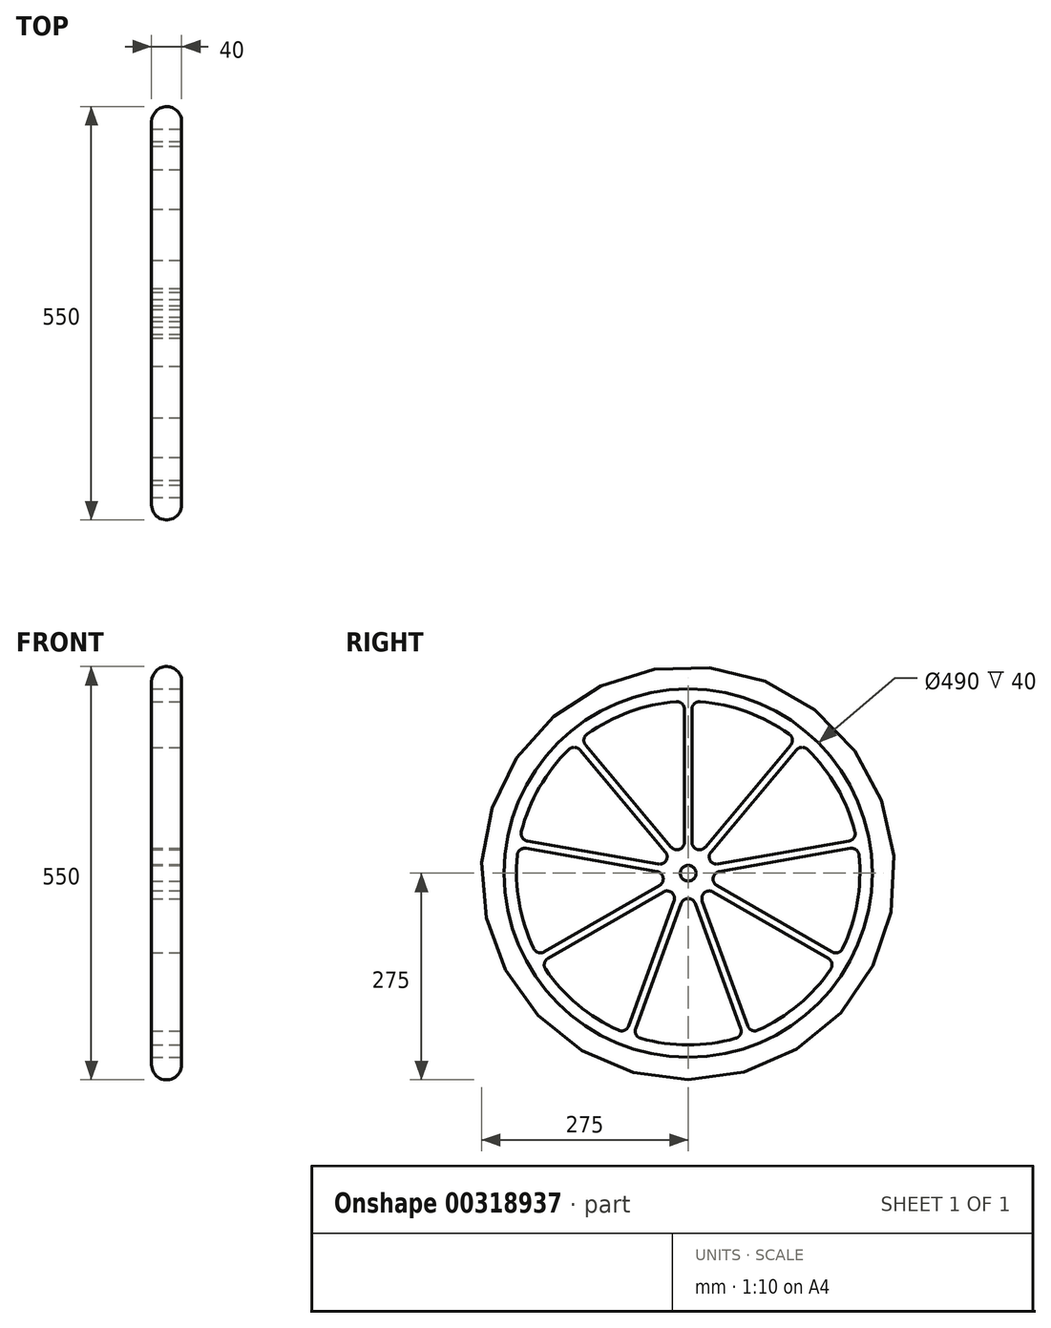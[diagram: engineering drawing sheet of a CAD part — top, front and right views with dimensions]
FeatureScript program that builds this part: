
annotation { "Feature Type Name" : "Feature", "Feature Type Description" : "" }
export const myFeature = defineFeature(function(context is Context, id is Id, definition is map)
    precondition{}
    {
        {
            var Q0;
            Q0=qCreatedBy(makeId("Front.planeOp"),FACE);
            var sketch = newSketch(context, id + "F0", { "sketchPlane" : qUnion([Q0])});
            skLineSegment(sketch, "E0.bottom", {"start": v(-20, 0) * mm, "end": v(20, 0) * mm});
            skLineSegment(sketch, "E0.top", {"start": v(-20, 245) * mm, "end": v(20, 245) * mm});
            skLineSegment(sketch, "E0.left", {"start": v(-20, 0) * mm, "end": v(-20, 245) * mm});
            skLineSegment(sketch, "E0.right", {"start": v(20, 0) * mm, "end": v(20, 245) * mm});
            skSolve(sketch);
        }
        {
            var Q0;
            Q0 = qSketchRegion(id + "F0", true);
            var Q1;
            Q1=sQuery(id+"F0.wireOp",EDGE,"E0.bottom");
            revolve(context, id + "F1", {"entities" : qUnion([Q0]), "axis" : qUnion([Q1]), "revolveType" : RevolveType.FULL});
        }
        {
            var Q0;
            Q0=makeQuery(id+"F1.opRevolve","SWEPT_FACE",FACE,{"disambiguationData":[OSD([sQuery(id+"F0.wireOp",EDGE,"E0.right")])]});
            var sketch = newSketch(context, id + "F2", { "sketchPlane" : qUnion([Q0])});
            skSolve(sketch);
        }
        {
            var Q0;
            Q0=makeQuery(id+"F2.imprint","IMPRINT",FACE,{"disambiguationData":[TD([[makeQuery(id+"F2.imprint","IMPRINT",EDGE,{"derivedFrom":makeQuery(id+"F1.opRevolve","SWEPT_EDGE",EDGE,{"disambiguationData":[OSD([sQuery(id+"F0.wireOp",EDGE,"E0.top"),sQuery(id+"F0.wireOp",EDGE,"E0.right")])]})}),-1.0]])]});
            var sketch = newSketch(context, id + "F3", { "sketchPlane" : qUnion([Q0])});
            skLineSegment(sketch, "E1", {"start": v(0, 0) * mm, "end": v(0, 260) * mm, "construction": true});
            skLineSegment(sketch, "E2", {"start": v(0, 0) * mm, "end": v(167.12, 199.17) * mm, "construction": true});
            skLineSegment(sketch, "E3", {"start": v(5, 218.19) * mm, "end": v(5, 41.21) * mm});
            skLineSegment(sketch, "E4", {"start": v(22.66, 34.78) * mm, "end": v(136.42, 170.36) * mm});
            skArc(sketch, "E5", {"start": v(134.58, 184.91) * mm, "mid": v(78.14, 214.68) * mm, "end": v(15.77, 228.16) * mm});
            skPoint(sketch, "E6.visualSharp", {"position": v(5, 13.74) * mm});
            skArc(sketch, "E6.filletArc", {"start": v(5, 41.21) * mm, "mid": v(11.58, 31.82) * mm, "end": v(22.66, 34.78) * mm});
            skPoint(sketch, "E7.visualSharp", {"position": v(143.2, 178.44) * mm});
            skArc(sketch, "E7.filletArc", {"start": v(136.42, 170.36) * mm, "mid": v(138.68, 178.04) * mm, "end": v(134.58, 184.91) * mm});
            skPoint(sketch, "E8.visualSharp", {"position": v(5, 228.74) * mm});
            skArc(sketch, "E8.filletArc", {"start": v(15.77, 228.16) * mm, "mid": v(8.2, 225.52) * mm, "end": v(5, 218.19) * mm});
            skArc(sketch, "E9.1.0", {"start": v(-15.77, 228.16) * mm, "mid": v(-78.14, 214.68) * mm, "end": v(-134.58, 184.91) * mm});
            skArc(sketch, "E9.1.1", {"start": v(-134.58, 184.91) * mm, "mid": v(-138.68, 178.04) * mm, "end": v(-136.42, 170.36) * mm});
            skLineSegment(sketch, "E9.1.2", {"start": v(-136.42, 170.36) * mm, "end": v(-22.66, 34.78) * mm});
            skArc(sketch, "E9.1.3", {"start": v(-5, 218.19) * mm, "mid": v(-8.2, 225.52) * mm, "end": v(-15.77, 228.16) * mm});
            skLineSegment(sketch, "E9.1.4", {"start": v(-5, 41.21) * mm, "end": v(-5, 218.19) * mm});
            skArc(sketch, "E9.1.5", {"start": v(-22.66, 34.78) * mm, "mid": v(-11.58, 31.82) * mm, "end": v(-5, 41.21) * mm});
            skPoint(sketch, "E9.1.6", {"position": v(-5, 13.74) * mm});
            skArc(sketch, "E9.2.0", {"start": v(-158.73, 164.64) * mm, "mid": v(-197.85, 114.23) * mm, "end": v(-221.95, 55.15) * mm});
            skArc(sketch, "E9.2.1", {"start": v(-221.95, 55.15) * mm, "mid": v(-220.67, 47.24) * mm, "end": v(-214, 42.81) * mm});
            skLineSegment(sketch, "E9.2.2", {"start": v(-214, 42.81) * mm, "end": v(-39.72, 12.08) * mm});
            skArc(sketch, "E9.2.3", {"start": v(-144.08, 163.93) * mm, "mid": v(-151.25, 167.49) * mm, "end": v(-158.73, 164.64) * mm});
            skLineSegment(sketch, "E9.2.4", {"start": v(-30.32, 28.36) * mm, "end": v(-144.08, 163.93) * mm});
            skArc(sketch, "E9.2.5", {"start": v(-39.72, 12.08) * mm, "mid": v(-29.32, 16.93) * mm, "end": v(-30.32, 28.36) * mm});
            skPoint(sketch, "E9.2.6", {"position": v(-12.66, 7.3) * mm});
            skArc(sketch, "E9.3.0", {"start": v(-227.43, 24.1) * mm, "mid": v(-224.98, -39.67) * mm, "end": v(-205.47, -100.43) * mm});
            skArc(sketch, "E9.3.1", {"start": v(-205.47, -100.43) * mm, "mid": v(-199.41, -105.66) * mm, "end": v(-191.46, -104.76) * mm});
            skLineSegment(sketch, "E9.3.2", {"start": v(-191.46, -104.76) * mm, "end": v(-38.2, -16.28) * mm});
            skArc(sketch, "E9.3.3", {"start": v(-215.74, 32.96) * mm, "mid": v(-223.52, 31.08) * mm, "end": v(-227.43, 24.1) * mm});
            skLineSegment(sketch, "E9.3.4", {"start": v(-41.45, 2.23) * mm, "end": v(-215.74, 32.96) * mm});
            skArc(sketch, "E9.3.5", {"start": v(-38.2, -16.28) * mm, "mid": v(-33.34, -5.88) * mm, "end": v(-41.45, 2.23) * mm});
            skPoint(sketch, "E9.3.6", {"position": v(-14.4, -2.54) * mm});
            skPoint(sketch, "E9.center", {"position": v(0, 0) * mm});
            skArc(sketch, "E10.1.4.0", {"start": v(-189.7, -127.73) * mm, "mid": v(-146.85, -175) * mm, "end": v(-92.85, -209) * mm});
            skArc(sketch, "E10.4.4.0", {"start": v(-92.85, -209) * mm, "mid": v(-84.84, -209.12) * mm, "end": v(-79.32, -203.32) * mm});
            skLineSegment(sketch, "E10.8.4.0", {"start": v(-79.32, -203.32) * mm, "end": v(-18.8, -37.02) * mm});
            skArc(sketch, "E10.11.4.0", {"start": v(-186.46, -113.42) * mm, "mid": v(-191.2, -119.87) * mm, "end": v(-189.7, -127.73) * mm});
            skLineSegment(sketch, "E10.15.4.0", {"start": v(-33.2, -24.94) * mm, "end": v(-186.46, -113.42) * mm});
            skArc(sketch, "E10.18.4.0", {"start": v(-18.8, -37.02) * mm, "mid": v(-21.76, -25.94) * mm, "end": v(-33.2, -24.94) * mm});
            skPoint(sketch, "E10.22.4.0", {"position": v(-9.4, -11.2) * mm});
            skArc(sketch, "E10.1.5.0", {"start": v(-63.22, -219.8) * mm, "mid": v(0, -228.45) * mm, "end": v(63.22, -219.8) * mm});
            skArc(sketch, "E10.4.5.0", {"start": v(63.22, -219.8) * mm, "mid": v(69.42, -214.73) * mm, "end": v(69.93, -206.74) * mm});
            skLineSegment(sketch, "E10.8.5.0", {"start": v(69.93, -206.74) * mm, "end": v(9.4, -40.44) * mm});
            skArc(sketch, "E10.11.5.0", {"start": v(-69.93, -206.74) * mm, "mid": v(-69.42, -214.73) * mm, "end": v(-63.22, -219.8) * mm});
            skLineSegment(sketch, "E10.15.5.0", {"start": v(-9.4, -40.44) * mm, "end": v(-69.93, -206.74) * mm});
            skArc(sketch, "E10.18.5.0", {"start": v(9.4, -40.44) * mm, "mid": v(0, -33.86) * mm, "end": v(-9.4, -40.44) * mm});
            skPoint(sketch, "E10.22.5.0", {"position": v(0, -14.62) * mm});
            skArc(sketch, "E11.1.6.0", {"start": v(92.85, -209) * mm, "mid": v(146.85, -175) * mm, "end": v(189.7, -127.73) * mm});
            skArc(sketch, "E11.4.6.0", {"start": v(189.7, -127.73) * mm, "mid": v(191.2, -119.87) * mm, "end": v(186.46, -113.42) * mm});
            skLineSegment(sketch, "E11.8.6.0", {"start": v(186.46, -113.42) * mm, "end": v(33.2, -24.94) * mm});
            skArc(sketch, "E11.11.6.0", {"start": v(79.32, -203.32) * mm, "mid": v(84.84, -209.12) * mm, "end": v(92.85, -209) * mm});
            skLineSegment(sketch, "E11.15.6.0", {"start": v(18.8, -37.02) * mm, "end": v(79.32, -203.32) * mm});
            skArc(sketch, "E11.18.6.0", {"start": v(33.2, -24.94) * mm, "mid": v(21.76, -25.94) * mm, "end": v(18.8, -37.02) * mm});
            skPoint(sketch, "E11.22.6.0", {"position": v(9.4, -11.2) * mm});
            skArc(sketch, "E11.1.7.0", {"start": v(205.47, -100.43) * mm, "mid": v(224.98, -39.67) * mm, "end": v(227.43, 24.1) * mm});
            skArc(sketch, "E11.4.7.0", {"start": v(227.43, 24.1) * mm, "mid": v(223.52, 31.08) * mm, "end": v(215.74, 32.96) * mm});
            skLineSegment(sketch, "E11.8.7.0", {"start": v(215.74, 32.96) * mm, "end": v(41.45, 2.23) * mm});
            skArc(sketch, "E11.11.7.0", {"start": v(191.46, -104.76) * mm, "mid": v(199.41, -105.66) * mm, "end": v(205.47, -100.43) * mm});
            skLineSegment(sketch, "E11.15.7.0", {"start": v(38.2, -16.28) * mm, "end": v(191.46, -104.76) * mm});
            skArc(sketch, "E11.18.7.0", {"start": v(41.45, 2.23) * mm, "mid": v(33.34, -5.88) * mm, "end": v(38.2, -16.28) * mm});
            skPoint(sketch, "E11.22.7.0", {"position": v(14.4, -2.54) * mm});
            skArc(sketch, "E11.1.8.0", {"start": v(221.95, 55.15) * mm, "mid": v(197.85, 114.23) * mm, "end": v(158.73, 164.64) * mm});
            skArc(sketch, "E11.4.8.0", {"start": v(158.73, 164.64) * mm, "mid": v(151.25, 167.49) * mm, "end": v(144.08, 163.93) * mm});
            skLineSegment(sketch, "E11.8.8.0", {"start": v(144.08, 163.93) * mm, "end": v(30.32, 28.36) * mm});
            skArc(sketch, "E11.11.8.0", {"start": v(214, 42.81) * mm, "mid": v(220.67, 47.24) * mm, "end": v(221.95, 55.15) * mm});
            skLineSegment(sketch, "E11.15.8.0", {"start": v(39.72, 12.08) * mm, "end": v(214, 42.81) * mm});
            skArc(sketch, "E11.18.8.0", {"start": v(30.32, 28.36) * mm, "mid": v(29.32, 16.93) * mm, "end": v(39.72, 12.08) * mm});
            skPoint(sketch, "E11.22.8.0", {"position": v(12.66, 7.3) * mm});
            skCircle(sketch, "E12", {"center": v(0, 0) * mm, "radius": 10.5 * mm});
            skSolve(sketch);
        }
        {
            var Q0;
            Q0 = qSketchRegion(id + "F3", true);
            extrude(context, id + "F4", {"entities" : qUnion([Q0]), "operationType" : NewBodyOperationType.REMOVE, "oppositeDirection" : true, "depth" : 79 * mm, "offsetDistance" : 25 * mm});
        }
        {
            var Q0;
            Q0=makeQuery(id+"F2.imprint","IMPRINT",FACE,{"disambiguationData":[TD([[makeQuery(id+"F2.imprint","IMPRINT",EDGE,{"derivedFrom":makeQuery(id+"F1.opRevolve","SWEPT_EDGE",EDGE,{"disambiguationData":[OSD([sQuery(id+"F0.wireOp",EDGE,"E0.top"),sQuery(id+"F0.wireOp",EDGE,"E0.right")])]})}),-1.0]])]});
            var sketch = newSketch(context, id + "F5", { "sketchPlane" : qUnion([Q0])});
            skCircle(sketch, "E13", {"center": v(0, 0) * mm, "radius": 275 * mm});
            skSolve(sketch);
        }
        {
            var Q0;
            Q0=makeQuery(id+"F5.imprint","IMPRINT",FACE,{"disambiguationData":[TD([[makeQuery(id+"F5.imprint","IMPRINT",EDGE,{"derivedFrom":sQuery(id+"F5.wireOp",EDGE,"E13")}),1.0]])]});
            extrude(context, id + "F6", {"entities" : qUnion([Q0]), "oppositeDirection" : true, "depth" : 40 * mm, "offsetDistance" : 25 * mm});
        }
        {
            var Q0;
            Q0=makeQuery(id+"F6.opExtrude","CAP_EDGE",EDGE,{"disambiguationData":[OSD([sQuery(id+"F5.wireOp",EDGE,"E13")])],"isStart":false});
            var Q1;
            Q1=makeQuery(id+"F6.opExtrude","CAP_EDGE",EDGE,{"disambiguationData":[OSD([sQuery(id+"F5.wireOp",EDGE,"E13")])],"isStart":true});
            fillet(context, id + "F7", {"entities" : qUnion([Q0, Q1]), "radius" : 20 * mm, "tangentPropagation" : true, "allowEdgeOverflow" : false});
        }
    });
